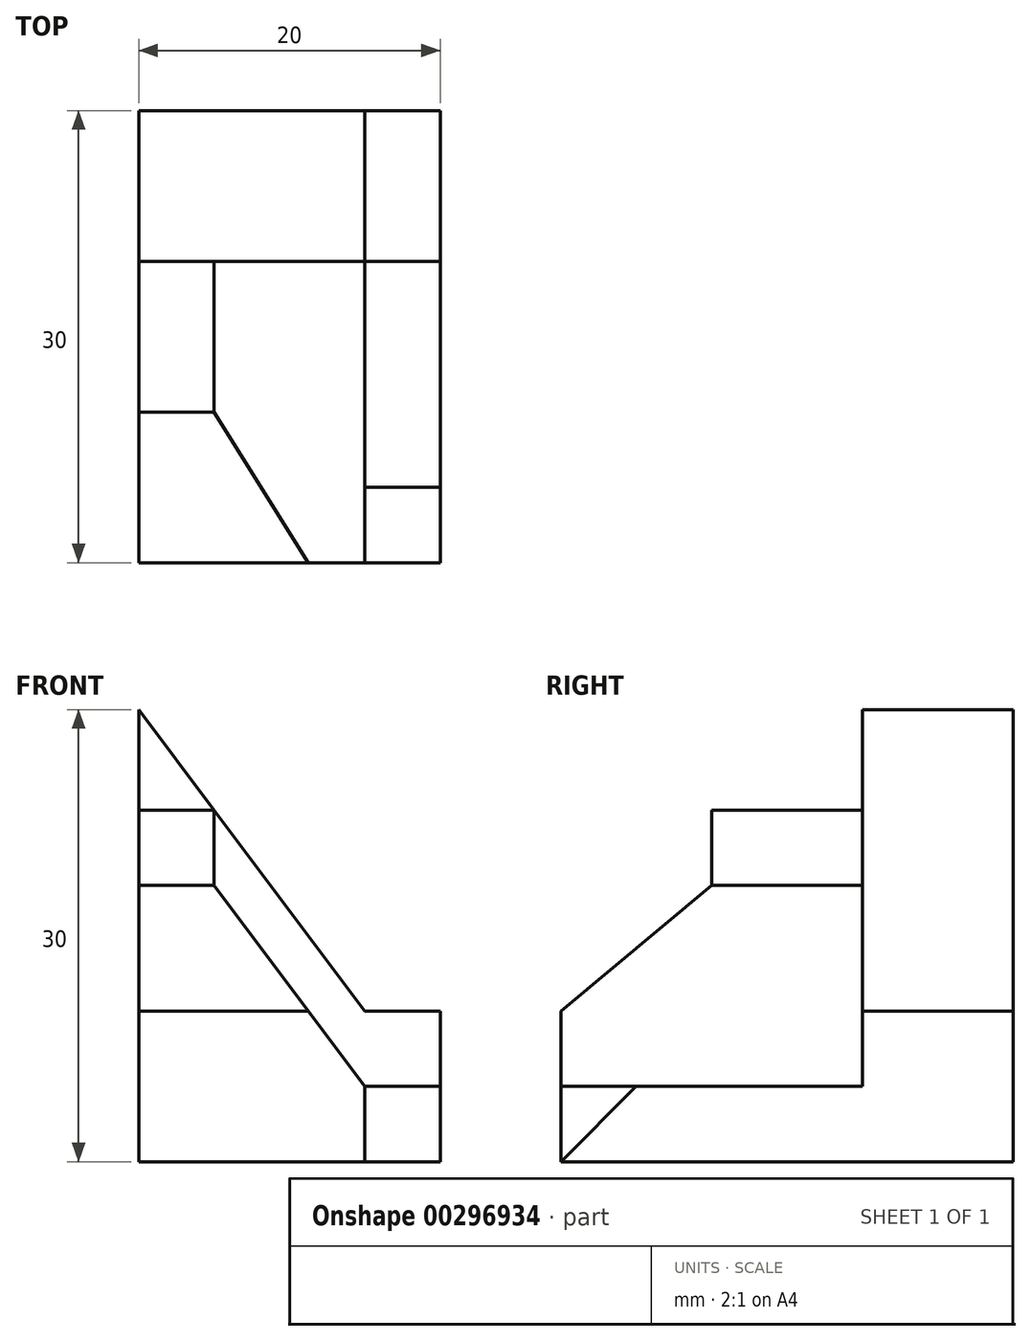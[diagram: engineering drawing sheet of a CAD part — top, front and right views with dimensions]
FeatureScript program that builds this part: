
annotation { "Feature Type Name" : "Feature", "Feature Type Description" : "" }
export const myFeature = defineFeature(function(context is Context, id is Id, definition is map)
    precondition{}
    {
        {
            var Q0;
            Q0=qCreatedBy(makeId("Front.planeOp"),FACE);
            var sketch = newSketch(context, id + "F0", { "sketchPlane" : qUnion([Q0])});
            skLineSegment(sketch, "E0.bottom", {"start": v(0, 0) * mm, "end": v(20, 0) * mm});
            skLineSegment(sketch, "E0.top", {"start": v(0, 30) * mm, "end": v(20, 30) * mm});
            skLineSegment(sketch, "E0.left", {"start": v(0, 0) * mm, "end": v(0, 30) * mm});
            skLineSegment(sketch, "E0.right", {"start": v(20, 0) * mm, "end": v(20, 30) * mm});
            skLineSegment(sketch, "E1", {"start": v(0, 30) * mm, "end": v(15, 10) * mm});
            skLineSegment(sketch, "E2", {"start": v(15, 10) * mm, "end": v(20, 10) * mm});
            skSolve(sketch);
        }
        {
            var Q0;
            {var subQ1=sQuery(id+"F0.wireOp",EDGE,"E0.bottom");Q0=makeQuery(id+"F0.imprint","IMPRINT",FACE,{"disambiguationData":[TD([[makeQuery(id+"F0.imprint","IMPRINT",EDGE,{"derivedFrom":subQ1}),1.0]])]});}
            extrude(context, id + "F1", {"entities" : qUnion([Q0]), "oppositeDirection" : true, "depth" : 30 * mm});
        }
        {
            var Q0;
            Q0=makeQuery(id+"F1.opExtrude","CAP_FACE",FACE,{"disambiguationData":[OSD([sQuery(id+"F0.wireOp",EDGE,"E0.bottom"),sQuery(id+"F0.wireOp",EDGE,"E0.left"),sQuery(id+"F0.wireOp",EDGE,"E0.right"),sQuery(id+"F0.wireOp",EDGE,"E1"),sQuery(id+"F0.wireOp",EDGE,"E2")])],"isStart":true});
            var sketch = newSketch(context, id + "F2", { "sketchPlane" : qUnion([Q0])});
            skLineSegment(sketch, "E3", {"start": v(0, 23.33) * mm, "end": v(5, 23.33) * mm});
            skLineSegment(sketch, "E4", {"start": v(5, 23.33) * mm, "end": v(5, 18.33) * mm});
            skLineSegment(sketch, "E5", {"start": v(5, 18.33) * mm, "end": v(15, 5) * mm});
            skLineSegment(sketch, "E6", {"start": v(15, 5) * mm, "end": v(20, 5) * mm});
            skSolve(sketch);
        }
        {
            var Q0;
            {var subQ0=sQuery(id+"F2.wireOp",EDGE,"E3");Q0=makeQuery(id+"F2.imprint","IMPRINT",FACE,{"disambiguationData":[TD([[makeQuery(id+"F2.imprint","IMPRINT",EDGE,{"derivedFrom":subQ0}),1.0]])]});}
            var Q1;
            {var subQ2=sQuery(id+"F2.wireOp",EDGE,"E4");Q1=makeQuery(id+"F2.imprint","IMPRINT",FACE,{"disambiguationData":[TD([[makeQuery(id+"F2.imprint","IMPRINT",EDGE,{"derivedFrom":subQ2}),1.0]])]});}
            extrude(context, id + "F3", {"entities" : qUnion([Q0, Q1]), "operationType" : NewBodyOperationType.REMOVE, "oppositeDirection" : true, "depth" : 20 * mm});
        }
        {
            var Q0;
            Q0=makeQuery(id+"F1.opExtrude","SWEPT_FACE",FACE,{"disambiguationData":[OSD([sQuery(id+"F0.wireOp",EDGE,"E0.left")])]});
            var sketch = newSketch(context, id + "F4", { "sketchPlane" : qUnion([Q0])});
            skLineSegment(sketch, "E7", {"start": v(-10, 23.33) * mm, "end": v(-10, 18.33) * mm});
            skLineSegment(sketch, "E8", {"start": v(-10, 18.33) * mm, "end": v(0, 10) * mm});
            skSolve(sketch);
        }
        {
            var Q0;
            {var subQ0=sQuery(id+"F4.wireOp",EDGE,"E7");Q0=makeQuery(id+"F4.imprint","IMPRINT",FACE,{"disambiguationData":[TD([[makeQuery(id+"F4.imprint","IMPRINT",EDGE,{"derivedFrom":subQ0}),1.0]])]});}
            extrude(context, id + "F5", {"entities" : qUnion([Q0]), "operationType" : NewBodyOperationType.REMOVE, "endBound" : BoundingType.THROUGH_ALL, "oppositeDirection" : true, "depth" : 25 * mm});
        }
        {
            var Q0;
            Q0=makeQuery(id+"F1.opExtrude","SWEPT_FACE",FACE,{"disambiguationData":[OSD([sQuery(id+"F0.wireOp",EDGE,"E0.right")])]});
            var sketch = newSketch(context, id + "F6", { "sketchPlane" : qUnion([Q0])});
            skLineSegment(sketch, "E9", {"start": v(0, 0) * mm, "end": v(5, 5) * mm});
            skSolve(sketch);
        }
        {
            var Q0;
            {var subQ0=sQuery(id+"F6.wireOp",EDGE,"E9");Q0=makeQuery(id+"F6.imprint","IMPRINT",FACE,{"disambiguationData":[TD([[makeQuery(id+"F6.imprint","IMPRINT",EDGE,{"derivedFrom":subQ0}),1.0]])]});}
            var Q1;
            Q1=makeQuery(id+"F3.boolean.opBoolean","COPY",VERTEX,{"derivedFrom":makeQuery(id+"F3.opExtrude","CAP_VERTEX",VERTEX,{"disambiguationData":[OSD([sQuery(id+"F2.wireOp",EDGE,"E5"),sQuery(id+"F2.wireOp",EDGE,"E6")])],"isStart":true})});
            extrude(context, id + "F7", {"entities" : qUnion([Q0]), "operationType" : NewBodyOperationType.REMOVE, "endBound" : BoundingType.UP_TO_VERTEX, "oppositeDirection" : true, "endBoundEntityVertex" : qUnion([Q1]), "depth" : 25 * mm});
        }
    });
